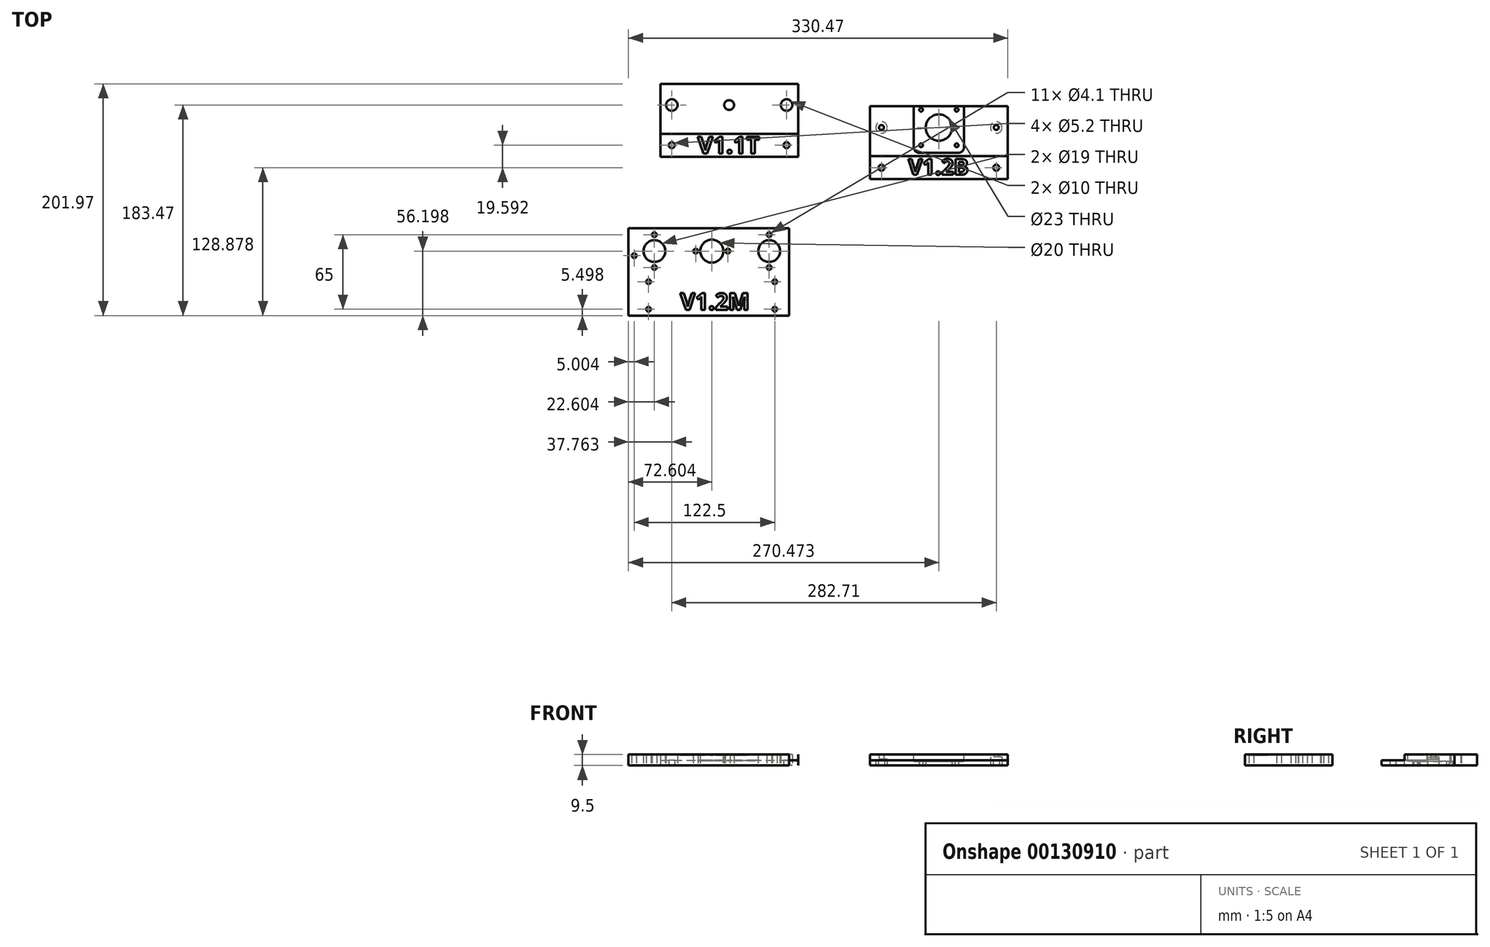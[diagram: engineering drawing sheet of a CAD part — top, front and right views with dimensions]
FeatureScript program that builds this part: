
annotation { "Feature Type Name" : "Feature", "Feature Type Description" : "" }
export const myFeature = defineFeature(function(context is Context, id is Id, definition is map)
    precondition{}
    {
        {
            var Q0;
            Q0=qCreatedBy(makeId("Top.planeOp"),FACE);
            var sketch = newSketch(context, id + "F0", { "sketchPlane" : qUnion([Q0])});
            skLineSegment(sketch, "E0.top", {"start": v(-68.7, -10) * mm, "end": v(51.3, -10) * mm});
            skLineSegment(sketch, "E1.bottom", {"start": v(-68.7, -10) * mm, "end": v(-58.7, -10) * mm, "construction": true});
            skLineSegment(sketch, "E1.top", {"start": v(-68.7, 0) * mm, "end": v(-58.7, 0) * mm, "construction": true});
            skLineSegment(sketch, "E1.left", {"start": v(-68.7, -10) * mm, "end": v(-68.7, 0) * mm});
            skLineSegment(sketch, "E1.right", {"start": v(-58.7, -10) * mm, "end": v(-58.7, 0) * mm, "construction": true});
            skLineSegment(sketch, "E2.bottom", {"start": v(51.3, -10) * mm, "end": v(41.3, -10) * mm, "construction": true});
            skLineSegment(sketch, "E2.top", {"start": v(51.3, 0) * mm, "end": v(41.3, 0) * mm, "construction": true});
            skLineSegment(sketch, "E2.left", {"start": v(51.3, -10) * mm, "end": v(51.3, 0) * mm});
            skLineSegment(sketch, "E2.right", {"start": v(41.3, -10) * mm, "end": v(41.3, 0) * mm, "construction": true});
            skLineSegment(sketch, "E3.bottom", {"start": v(-68.7, 45) * mm, "end": v(-58.7, 45) * mm, "construction": true});
            skLineSegment(sketch, "E3.top", {"start": v(-68.7, 35) * mm, "end": v(-58.7, 35) * mm, "construction": true});
            skLineSegment(sketch, "E3.right", {"start": v(-58.7, 45) * mm, "end": v(-58.7, 35) * mm, "construction": true});
            skLineSegment(sketch, "E4", {"start": v(-58.7, 35) * mm, "end": v(-8.7, 35) * mm, "construction": true});
            skLineSegment(sketch, "E5", {"start": v(-8.7, 35) * mm, "end": v(41.3, 35) * mm, "construction": true});
            skLineSegment(sketch, "E6", {"start": v(-58.7, 35) * mm, "end": v(-58.7, 0) * mm});
            skCircle(sketch, "E7", {"center": v(-8.7, 35) * mm, "radius": 4.25 * mm});
            skCircle(sketch, "E8", {"center": v(-58.7, 35) * mm, "radius": 5 * mm});
            skCircle(sketch, "E9", {"center": v(41.3, 35) * mm, "radius": 5 * mm});
            skCircle(sketch, "E10", {"center": v(41.3, 0) * mm, "radius": 2.6 * mm});
            skCircle(sketch, "E11", {"center": v(-58.7, 0) * mm, "radius": 2.6 * mm});
            skLineSegment(sketch, "E12", {"start": v(51.3, 0) * mm, "end": v(51.3, 10) * mm});
            skPoint(sketch, "E12.endSnap0", {"position": v(51.3, -5) * mm});
            skLineSegment(sketch, "E13", {"start": v(51.3, 10) * mm, "end": v(-68.7, 10) * mm});
            skLineSegment(sketch, "E14", {"start": v(-68.7, 10) * mm, "end": v(-68.7, 0) * mm});
            skLineSegment(sketch, "E15", {"start": v(51.3, 10) * mm, "end": v(51.3, 53.5) * mm});
            skLineSegment(sketch, "E16", {"start": v(51.3, 53.5) * mm, "end": v(-68.7, 53.5) * mm});
            skLineSegment(sketch, "E17", {"start": v(-68.7, 53.5) * mm, "end": v(-68.7, 10) * mm});
            skSolve(sketch);
        }
        {
            var Q0;
            Q0 = qSketchRegion(id + "F0", true);
            extrude(context, id + "F1", {"entities" : qUnion([Q0]), "depth" : 4.5 * mm});
        }
        {
            var Q0;
            Q0=makeQuery(id+"F1.opExtrude","CAP_FACE",FACE,{"disambiguationData":[OSD([sQuery(id+"F0.wireOp",EDGE,"E0.bottom"),sQuery(id+"F0.wireOp",EDGE,"E0.top"),sQuery(id+"F0.wireOp",EDGE,"E0.left"),sQuery(id+"F0.wireOp",EDGE,"E0.right"),sQuery(id+"F0.wireOp",EDGE,"E7"),sQuery(id+"F0.wireOp",EDGE,"E8"),sQuery(id+"F0.wireOp",EDGE,"E9"),sQuery(id+"F0.wireOp",EDGE,"E10"),sQuery(id+"F0.wireOp",EDGE,"E11")])],"isStart":false});
            var sketch = newSketch(context, id + "F2", { "sketchPlane" : qUnion([Q0])});
            skLineSegment(sketch, "E18.top", {"start": v(-68.7, 10) * mm, "end": v(51.3, 10) * mm});
            skLineSegment(sketch, "E18.left", {"start": v(-68.7, 53.5) * mm, "end": v(-68.7, 10) * mm});
            skLineSegment(sketch, "E18.right", {"start": v(51.3, 53.5) * mm, "end": v(51.3, 10) * mm});
            skCircle(sketch, "E19.0", {"center": v(-58.7, 35) * mm, "radius": 5 * mm});
            skCircle(sketch, "E20.0", {"center": v(-8.7, 35) * mm, "radius": 4.25 * mm});
            skCircle(sketch, "E21.0.0", {"center": v(41.3, 35) * mm, "radius": 5 * mm});
            skLineSegment(sketch, "E22", {"start": v(-68.7, 53.5) * mm, "end": v(51.3, 53.5) * mm});
            skSolve(sketch);
        }
        {
            var Q0;
            Q0 = qSketchRegion(id + "F2", true);
            extrude(context, id + "F3", {"entities" : qUnion([Q0]), "operationType" : NewBodyOperationType.ADD, "depth" : 5 * mm});
        }
        {
            var Q0;
            Q0=qCreatedBy(makeId("Top.planeOp"),FACE);
            var sketch = newSketch(context, id + "F4", { "sketchPlane" : qUnion([Q0])});
            skLineSegment(sketch, "E23.bottom", {"start": v(-96.47, -72.27) * mm, "end": v(38.53, -72.27) * mm});
            skLineSegment(sketch, "E23.top", {"start": v(-96.47, -148.47) * mm, "end": v(38.53, -148.47) * mm});
            skLineSegment(sketch, "E23.left", {"start": v(-96.47, -72.27) * mm, "end": v(-96.47, -148.47) * mm});
            skLineSegment(sketch, "E23.right", {"start": v(38.53, -72.27) * mm, "end": v(38.53, -148.47) * mm});
            skLineSegment(sketch, "E24.bottom", {"start": v(38.53, -148.47) * mm, "end": v(31.03, -148.47) * mm, "construction": true});
            skLineSegment(sketch, "E24.top", {"start": v(38.53, -142.97) * mm, "end": v(31.03, -142.97) * mm, "construction": true});
            skLineSegment(sketch, "E24.left", {"start": v(38.53, -148.47) * mm, "end": v(38.53, -142.97) * mm, "construction": true});
            skLineSegment(sketch, "E24.right", {"start": v(31.03, -148.47) * mm, "end": v(31.03, -142.97) * mm, "construction": true});
            skLineSegment(sketch, "E25", {"start": v(31.03, -142.97) * mm, "end": v(31.03, -118.97) * mm, "construction": true});
            skCircle(sketch, "E26", {"center": v(31.03, -118.97) * mm, "radius": 2.05 * mm});
            skCircle(sketch, "E27", {"center": v(31.03, -142.97) * mm, "radius": 2.05 * mm});
            skLineSegment(sketch, "E28", {"start": v(38.53, -72.27) * mm, "end": v(26.13, -72.27) * mm, "construction": true});
            skLineSegment(sketch, "E29", {"start": v(26.13, -72.27) * mm, "end": v(26.13, -77.97) * mm, "construction": true});
            skLineSegment(sketch, "E30", {"start": v(26.13, -77.97) * mm, "end": v(26.13, -106.57) * mm, "construction": true});
            skPoint(sketch, "E31", {"position": v(26.13, -92.27) * mm});
            skCircle(sketch, "E32", {"center": v(26.13, -77.97) * mm, "radius": 2.05 * mm});
            skCircle(sketch, "E33", {"center": v(26.13, -106.57) * mm, "radius": 2.05 * mm});
            skCircle(sketch, "E34", {"center": v(26.13, -92.27) * mm, "radius": 9.5 * mm});
            skLineSegment(sketch, "E35", {"start": v(26.13, -72.27) * mm, "end": v(-23.87, -72.27) * mm, "construction": true});
            skLineSegment(sketch, "E36", {"start": v(-23.87, -72.27) * mm, "end": v(-23.87, -92.27) * mm, "construction": true});
            skLineSegment(sketch, "E37", {"start": v(-37.87, -92.27) * mm, "end": v(-9.87, -92.27) * mm, "construction": true});
            skCircle(sketch, "E38", {"center": v(-9.87, -92.27) * mm, "radius": 2.05 * mm});
            skCircle(sketch, "E39", {"center": v(-37.87, -92.27) * mm, "radius": 2.05 * mm});
            skCircle(sketch, "E40", {"center": v(-23.87, -92.27) * mm, "radius": 10 * mm});
            skLineSegment(sketch, "E41", {"start": v(-96.47, -148.47) * mm, "end": v(-78.97, -148.47) * mm, "construction": true});
            skLineSegment(sketch, "E42", {"start": v(-78.97, -148.47) * mm, "end": v(-78.97, -118.97) * mm, "construction": true});
            skCircle(sketch, "E43", {"center": v(-78.97, -118.97) * mm, "radius": 2.05 * mm});
            skLineSegment(sketch, "E44", {"start": v(-78.97, -148.47) * mm, "end": v(-78.97, -142.97) * mm, "construction": true});
            skCircle(sketch, "E45", {"center": v(-78.97, -142.97) * mm, "radius": 2.05 * mm});
            skLineSegment(sketch, "E46", {"start": v(-96.47, -72.27) * mm, "end": v(-73.87, -72.27) * mm, "construction": true});
            skLineSegment(sketch, "E47", {"start": v(-73.87, -72.27) * mm, "end": v(-73.87, -92.27) * mm, "construction": true});
            skLineSegment(sketch, "E48", {"start": v(-73.87, -72.27) * mm, "end": v(-73.87, -77.97) * mm, "construction": true});
            skLineSegment(sketch, "E49", {"start": v(-73.87, -77.97) * mm, "end": v(-73.87, -106.57) * mm, "construction": true});
            skCircle(sketch, "E50", {"center": v(-73.87, -106.57) * mm, "radius": 2.05 * mm});
            skCircle(sketch, "E51", {"center": v(-73.87, -77.97) * mm, "radius": 2.05 * mm});
            skCircle(sketch, "E52", {"center": v(-73.87, -92.27) * mm, "radius": 9.5 * mm});
            skLineSegment(sketch, "E53", {"start": v(-96.47, -72.27) * mm, "end": v(-91.47, -72.27) * mm, "construction": true});
            skLineSegment(sketch, "E54", {"start": v(-91.47, -72.27) * mm, "end": v(-91.47, -96.27) * mm, "construction": true});
            skCircle(sketch, "E55", {"center": v(-91.47, -96.27) * mm, "radius": 2.05 * mm});
            skSolve(sketch);
        }
        {
            var Q0;
            Q0 = qSketchRegion(id + "F4", true);
            extrude(context, id + "F5", {"entities" : qUnion([Q0]), "depth" : 9.5 * mm});
        }
        {
            var Q0;
            Q0=qCreatedBy(makeId("Top.planeOp"),FACE);
            var sketch = newSketch(context, id + "F6", { "sketchPlane" : qUnion([Q0])});
            skLineSegment(sketch, "E56.bottom", {"start": v(114, 33.9) * mm, "end": v(234, 33.9) * mm});
            skLineSegment(sketch, "E56.top", {"start": v(114, -29.6) * mm, "end": v(234, -29.6) * mm});
            skLineSegment(sketch, "E56.left", {"start": v(114, 33.9) * mm, "end": v(114, -29.6) * mm});
            skLineSegment(sketch, "E56.right", {"start": v(234, 33.9) * mm, "end": v(234, -29.6) * mm});
            skLineSegment(sketch, "E57", {"start": v(114, -29.6) * mm, "end": v(114, -19.6) * mm, "construction": true});
            skLineSegment(sketch, "E58", {"start": v(114, -19.6) * mm, "end": v(124, -19.6) * mm, "construction": true});
            skLineSegment(sketch, "E59", {"start": v(124, -19.6) * mm, "end": v(224, -19.6) * mm, "construction": true});
            skLineSegment(sketch, "E60", {"start": v(224, -19.6) * mm, "end": v(224, 15.4) * mm, "construction": true});
            skLineSegment(sketch, "E61", {"start": v(114, 33.9) * mm, "end": v(124, 33.9) * mm, "construction": true});
            skLineSegment(sketch, "E62", {"start": v(124, 33.9) * mm, "end": v(124, 15.4) * mm, "construction": true});
            skLineSegment(sketch, "E63", {"start": v(124, 33.9) * mm, "end": v(152, 33.9) * mm, "construction": true});
            skLineSegment(sketch, "E64", {"start": v(152, 33.9) * mm, "end": v(158.5, 33.9) * mm, "construction": true});
            skLineSegment(sketch, "E65", {"start": v(114, -19.6) * mm, "end": v(114, -9.6) * mm, "construction": true});
            skLineSegment(sketch, "E66", {"start": v(114, -9.6) * mm, "end": v(234, -9.6) * mm, "construction": true});
            skLineSegment(sketch, "E67", {"start": v(158.5, -9.6) * mm, "end": v(158.5, -0.1) * mm, "construction": true});
            skLineSegment(sketch, "E68", {"start": v(158.5, -0.1) * mm, "end": v(189.5, -0.1) * mm, "construction": true});
            skLineSegment(sketch, "E69", {"start": v(189.5, -0.1) * mm, "end": v(189.5, 30.9) * mm, "construction": true});
            skLineSegment(sketch, "E70", {"start": v(189.5, 30.9) * mm, "end": v(158.5, 30.9) * mm, "construction": true});
            skLineSegment(sketch, "E71", {"start": v(158.5, 30.9) * mm, "end": v(174, 30.9) * mm, "construction": true});
            skLineSegment(sketch, "E72", {"start": v(174, 30.9) * mm, "end": v(174, 15.4) * mm, "construction": true});
            skCircle(sketch, "E73", {"center": v(158.5, 30.9) * mm, "radius": 1.6 * mm});
            skCircle(sketch, "E74", {"center": v(189.5, 30.9) * mm, "radius": 1.6 * mm});
            skCircle(sketch, "E75", {"center": v(158.5, -0.1) * mm, "radius": 1.6 * mm});
            skCircle(sketch, "E76", {"center": v(189.5, -0.1) * mm, "radius": 1.6 * mm});
            skCircle(sketch, "E77", {"center": v(174, 15.4) * mm, "radius": 11.5 * mm});
            skCircle(sketch, "E78", {"center": v(224, -19.6) * mm, "radius": 2.6 * mm});
            skCircle(sketch, "E79", {"center": v(124, -19.6) * mm, "radius": 2.6 * mm});
            skCircle(sketch, "E80", {"center": v(224, 15.4) * mm, "radius": 2.1 * mm});
            skCircle(sketch, "E81", {"center": v(124, 15.4) * mm, "radius": 2.1 * mm});
            skPoint(sketch, "E82", {"position": v(189.5, 15.4) * mm});
            skSolve(sketch);
        }
        {
            var Q0;
            Q0 = qSketchRegion(id + "F6", true);
            extrude(context, id + "F7", {"entities" : qUnion([Q0]), "depth" : 4.5 * mm});
        }
        {
            var Q0;
            Q0=makeQuery(id+"F7.opExtrude","CAP_FACE",FACE,{"disambiguationData":[OSD([sQuery(id+"F6.wireOp",EDGE,"E56.bottom"),sQuery(id+"F6.wireOp",EDGE,"E56.top"),sQuery(id+"F6.wireOp",EDGE,"E56.left"),sQuery(id+"F6.wireOp",EDGE,"E56.right"),sQuery(id+"F6.wireOp",EDGE,"E73"),sQuery(id+"F6.wireOp",EDGE,"E74"),sQuery(id+"F6.wireOp",EDGE,"E75"),sQuery(id+"F6.wireOp",EDGE,"E76"),sQuery(id+"F6.wireOp",EDGE,"E77"),sQuery(id+"F6.wireOp",EDGE,"E78"),sQuery(id+"F6.wireOp",EDGE,"E79"),sQuery(id+"F6.wireOp",EDGE,"E80"),sQuery(id+"F6.wireOp",EDGE,"E81")])],"isStart":false});
            var sketch = newSketch(context, id + "F8", { "sketchPlane" : qUnion([Q0])});
            skLineSegment(sketch, "E83.bottom", {"start": v(114, 33.9) * mm, "end": v(234, 33.9) * mm});
            skLineSegment(sketch, "E83.top", {"start": v(114, -9.6) * mm, "end": v(234, -9.6) * mm});
            skLineSegment(sketch, "E83.left", {"start": v(114, 33.9) * mm, "end": v(114, -9.6) * mm});
            skLineSegment(sketch, "E83.right", {"start": v(234, 33.9) * mm, "end": v(234, -9.6) * mm});
            skCircle(sketch, "E84.0", {"center": v(124, 15.4) * mm, "radius": 2.1 * mm});
            skCircle(sketch, "E85.0", {"center": v(158.5, 30.9) * mm, "radius": 1.6 * mm});
            skCircle(sketch, "E86.0", {"center": v(158.5, -0.1) * mm, "radius": 1.6 * mm});
            skCircle(sketch, "E87.0", {"center": v(174, 15.4) * mm, "radius": 11.5 * mm});
            skCircle(sketch, "E88.0", {"center": v(189.5, 30.9) * mm, "radius": 1.6 * mm});
            skCircle(sketch, "E89.0", {"center": v(189.5, -0.1) * mm, "radius": 1.6 * mm});
            skCircle(sketch, "E90.0", {"center": v(224, 15.4) * mm, "radius": 2.1 * mm});
            skSolve(sketch);
        }
        {
            var Q0;
            Q0 = qSketchRegion(id + "F8", true);
            extrude(context, id + "F9", {"entities" : qUnion([Q0]), "operationType" : NewBodyOperationType.ADD, "depth" : 5 * mm});
        }
        {
            var Q0;
            Q0=makeQuery(id+"F6.imprint","IMPRINT",FACE,{"disambiguationData":[TD([[makeQuery(id+"F6.imprint","IMPRINT",EDGE,{"derivedFrom":sQuery(id+"F6.wireOp",EDGE,"E56.bottom")}),-1.0]])]});
            var sketch = newSketch(context, id + "F10", { "sketchPlane" : qUnion([Q0])});
            skCircle(sketch, "E91", {"center": v(124, 15.4) * mm, "radius": 5 * mm});
            skCircle(sketch, "E92", {"center": v(224, 15.4) * mm, "radius": 5 * mm});
            skSolve(sketch);
        }
        {
            var Q0;
            Q0 = qSketchRegion(id + "F10", true);
            extrude(context, id + "F11", {"entities" : qUnion([Q0]), "operationType" : NewBodyOperationType.REMOVE, "depth" : 7.5 * mm});
        }
        {
            var Q0;
            Q0=makeQuery(id+"F9.opExtrude","CAP_FACE",FACE,{"disambiguationData":[OSD([sQuery(id+"F8.wireOp",EDGE,"E83.bottom"),sQuery(id+"F8.wireOp",EDGE,"E83.top"),sQuery(id+"F8.wireOp",EDGE,"E83.left"),sQuery(id+"F8.wireOp",EDGE,"E83.right"),sQuery(id+"F8.wireOp",EDGE,"E84.0"),sQuery(id+"F8.wireOp",EDGE,"E85.0"),sQuery(id+"F8.wireOp",EDGE,"E86.0"),sQuery(id+"F8.wireOp",EDGE,"E87.0"),sQuery(id+"F8.wireOp",EDGE,"E88.0"),sQuery(id+"F8.wireOp",EDGE,"E89.0"),sQuery(id+"F8.wireOp",EDGE,"E90.0")])],"isStart":false});
            var sketch = newSketch(context, id + "F12", { "sketchPlane" : qUnion([Q0])});
            skPoint(sketch, "E93.0", {"position": v(152, 33.9) * mm});
            skLineSegment(sketch, "E94", {"start": v(152, 33.9) * mm, "end": v(114, 33.9) * mm});
            skLineSegment(sketch, "E95", {"start": v(152, 33.9) * mm, "end": v(152, -1.6) * mm});
            skLineSegment(sketch, "E96", {"start": v(157, -6.6) * mm, "end": v(191, -6.6) * mm});
            skLineSegment(sketch, "E97", {"start": v(196, -1.6) * mm, "end": v(196, 33.9) * mm});
            skPoint(sketch, "E98.visualSharp", {"position": v(152, -6.6) * mm});
            skArc(sketch, "E98.filletArc", {"start": v(152, -1.6) * mm, "mid": v(153.47, -5.13) * mm, "end": v(157, -6.6) * mm});
            skPoint(sketch, "E99.visualSharp", {"position": v(196, -6.6) * mm});
            skArc(sketch, "E99.filletArc", {"start": v(191, -6.6) * mm, "mid": v(194.54, -5.13) * mm, "end": v(196, -1.6) * mm});
            skLineSegment(sketch, "E100", {"start": v(152, 33.9) * mm, "end": v(196, 33.9) * mm});
            skSolve(sketch);
        }
        {
            var Q0;
            Q0 = qSketchRegion(id + "F12", true);
            extrude(context, id + "F13", {"entities" : qUnion([Q0]), "operationType" : NewBodyOperationType.REMOVE, "oppositeDirection" : true, "depth" : 6 * mm});
        }
        {
            var Q0;
            Q0=makeQuery(id+"F1.opExtrude","CAP_FACE",FACE,{"disambiguationData":[OSD([sQuery(id+"F0.wireOp",EDGE,"E0.bottom"),sQuery(id+"F0.wireOp",EDGE,"E0.top"),sQuery(id+"F0.wireOp",EDGE,"E0.left"),sQuery(id+"F0.wireOp",EDGE,"E0.right"),sQuery(id+"F0.wireOp",EDGE,"E7"),sQuery(id+"F0.wireOp",EDGE,"E8"),sQuery(id+"F0.wireOp",EDGE,"E9"),sQuery(id+"F0.wireOp",EDGE,"E10"),sQuery(id+"F0.wireOp",EDGE,"E11")])],"isStart":false});
            var sketch = newSketch(context, id + "F14", { "sketchPlane" : qUnion([Q0])});
            skText(sketch, "E101", { "text": "V1.1T", "fontName": "OpenSans-Bold.ttf"});
            const initialGuessF14  = {"E101": [-0.03614, -0.00712, 1, 0, 0.01468]};
            skSetInitialGuess(sketch, initialGuessF14);
            skSolve(sketch);
        }
        {
            var Q0;
            Q0 = qSketchRegion(id + "F14", true);
            extrude(context, id + "F15", {"entities" : qUnion([Q0]), "operationType" : NewBodyOperationType.REMOVE, "oppositeDirection" : true, "depth" : .4 * mm});
        }
        {
            var Q0;
            Q0=makeQuery(id+"F5.opExtrude","CAP_FACE",FACE,{"disambiguationData":[OSD([sQuery(id+"F4.wireOp",EDGE,"E23.bottom"),sQuery(id+"F4.wireOp",EDGE,"E23.top"),sQuery(id+"F4.wireOp",EDGE,"E23.left"),sQuery(id+"F4.wireOp",EDGE,"E23.right"),sQuery(id+"F4.wireOp",EDGE,"E26"),sQuery(id+"F4.wireOp",EDGE,"E27"),sQuery(id+"F4.wireOp",EDGE,"E32"),sQuery(id+"F4.wireOp",EDGE,"E33"),sQuery(id+"F4.wireOp",EDGE,"E34"),sQuery(id+"F4.wireOp",EDGE,"E38"),sQuery(id+"F4.wireOp",EDGE,"E39"),sQuery(id+"F4.wireOp",EDGE,"E40"),sQuery(id+"F4.wireOp",EDGE,"E43"),sQuery(id+"F4.wireOp",EDGE,"E45"),sQuery(id+"F4.wireOp",EDGE,"E50"),sQuery(id+"F4.wireOp",EDGE,"E51"),sQuery(id+"F4.wireOp",EDGE,"E52"),sQuery(id+"F4.wireOp",EDGE,"E55")])],"isStart":false});
            var sketch = newSketch(context, id + "F16", { "sketchPlane" : qUnion([Q0])});
            skText(sketch, "E102", { "text": "V1.2M", "fontName": "OpenSans-Bold.ttf"});
            const initialGuessF16  = {"E102": [-0.0513, -0.14332, 1, 0, 0.01443]};
            skSetInitialGuess(sketch, initialGuessF16);
            skSolve(sketch);
        }
        {
            var Q0;
            Q0 = qSketchRegion(id + "F16", true);
            extrude(context, id + "F17", {"entities" : qUnion([Q0]), "operationType" : NewBodyOperationType.REMOVE, "oppositeDirection" : true, "depth" : .4 * mm});
        }
        {
            var Q0;
            Q0=makeQuery(id+"F7.opExtrude","CAP_FACE",FACE,{"disambiguationData":[OSD([sQuery(id+"F6.wireOp",EDGE,"E56.bottom"),sQuery(id+"F6.wireOp",EDGE,"E56.top"),sQuery(id+"F6.wireOp",EDGE,"E56.left"),sQuery(id+"F6.wireOp",EDGE,"E56.right"),sQuery(id+"F6.wireOp",EDGE,"E73"),sQuery(id+"F6.wireOp",EDGE,"E74"),sQuery(id+"F6.wireOp",EDGE,"E75"),sQuery(id+"F6.wireOp",EDGE,"E76"),sQuery(id+"F6.wireOp",EDGE,"E77"),sQuery(id+"F6.wireOp",EDGE,"E78"),sQuery(id+"F6.wireOp",EDGE,"E79"),sQuery(id+"F6.wireOp",EDGE,"E80"),sQuery(id+"F6.wireOp",EDGE,"E81")])],"isStart":false});
            var sketch = newSketch(context, id + "F18", { "sketchPlane" : qUnion([Q0])});
            skText(sketch, "E103", { "text": "V1.2B", "fontName": "OpenSans-Bold.ttf"});
            const initialGuessF18  = {"E103": [0.14724, -0.0257, 1, 0, 0.01377]};
            skSetInitialGuess(sketch, initialGuessF18);
            skSolve(sketch);
        }
        {
            var Q0;
            Q0 = qSketchRegion(id + "F18", true);
            extrude(context, id + "F19", {"entities" : qUnion([Q0]), "operationType" : NewBodyOperationType.REMOVE, "oppositeDirection" : true, "depth" : .4 * mm});
        }
        {
            var Q0;
            Q0=makeQuery(id+"F11.boolean.opBoolean","COPY",FACE,{"derivedFrom":makeQuery(id+"F11.opExtrude","CAP_FACE",FACE,{"disambiguationData":[OSD([sQuery(id+"F10.wireOp",EDGE,"E91")])],"isStart":false})});
            extrude(context, id + "F20", {"entities" : qUnion([Q0]), "operationType" : NewBodyOperationType.ADD, "depth" : 2 * mm});
        }
        {
            var Q0;
            Q0=makeQuery(id+"F5.opExtrude","SWEPT_FACE",FACE,{"disambiguationData":[OSD([sQuery(id+"F4.wireOp",EDGE,"E23.right")])]});
            extrude(context, id + "F21", {"entities" : qUnion([Q0]), "operationType" : NewBodyOperationType.ADD, "depth" : 5 * mm});
        }
    });
